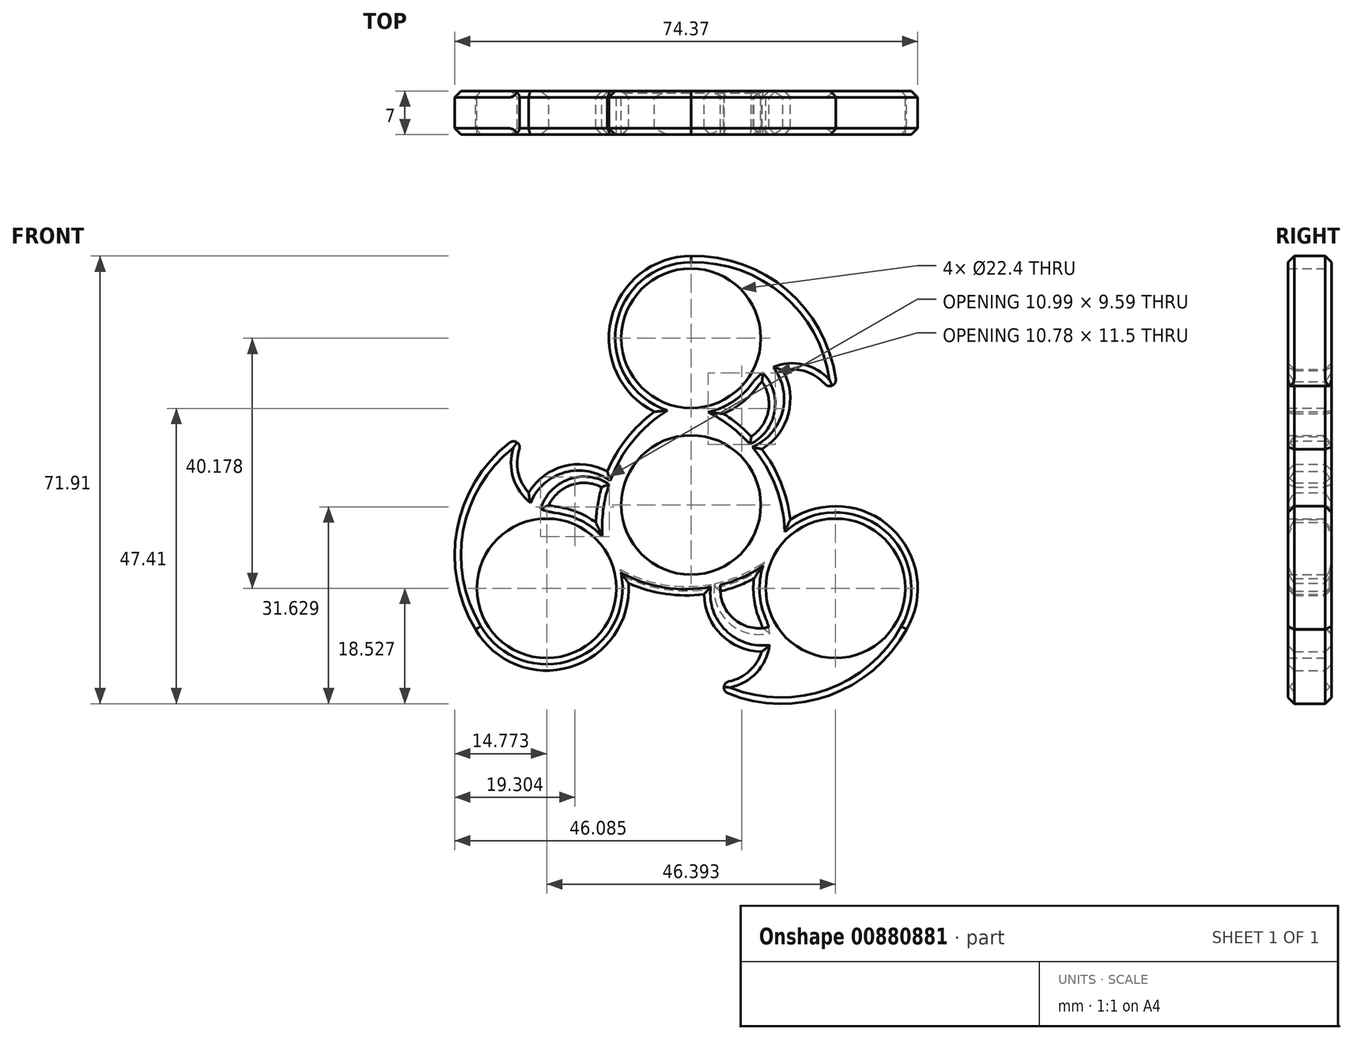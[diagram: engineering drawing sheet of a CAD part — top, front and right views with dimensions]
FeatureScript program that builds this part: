
annotation { "Feature Type Name" : "Feature", "Feature Type Description" : "" }
export const myFeature = defineFeature(function(context is Context, id is Id, definition is map)
    precondition{}
    {
        {
            var Q0;
            Q0=qCreatedBy(makeId("Front.planeOp"),FACE);
            var sketch = newSketch(context, id + "F0", { "sketchPlane" : qUnion([Q0])});
            skCircle(sketch, "E0", {"center": v(0, 0) * mm, "radius": 11.2 * mm});
            skCircle(sketch, "E1", {"center": v(0, 26.79) * mm, "radius": 13.2 * mm});
            skCircle(sketch, "E2", {"center": v(0, 26.79) * mm, "radius": 11.2 * mm});
            skCircle(sketch, "E3.1.0", {"center": v(-23.2, -13.4) * mm, "radius": 11.2 * mm});
            skCircle(sketch, "E3.1.1", {"center": v(-23.2, -13.4) * mm, "radius": 13.2 * mm});
            skCircle(sketch, "E3.2.0", {"center": v(23.2, -13.4) * mm, "radius": 11.2 * mm});
            skCircle(sketch, "E3.2.1", {"center": v(23.2, -13.4) * mm, "radius": 13.2 * mm});
            skArc(sketch, "E4", {"start": v(15.92, -2.38) * mm, "mid": v(12.5, 7.36) * mm, "end": v(5.2, 14.65) * mm});
            skArc(sketch, "E5.1.0", {"start": v(-5.9, 14.98) * mm, "mid": v(-12.62, 7.15) * mm, "end": v(-15.29, -2.82) * mm});
            skArc(sketch, "E5.2.0", {"start": v(-10.02, -12.6) * mm, "mid": v(0.12, -14.5) * mm, "end": v(10.09, -11.83) * mm});
            skArc(sketch, "E6", {"start": v(23.3, 14.22) * mm, "mid": v(17.54, 32.43) * mm, "end": v(0, 39.99) * mm});
            skArc(sketch, "E7", {"start": v(23.3, 14.22) * mm, "mid": v(18.73, 21.33) * mm, "end": v(10.62, 18.95) * mm});
            skArc(sketch, "E8.1.0", {"start": v(-23.97, 13.07) * mm, "mid": v(-27.83, 5.56) * mm, "end": v(-21.72, -0.28) * mm});
            skArc(sketch, "E8.1.1", {"start": v(-23.97, 13.07) * mm, "mid": v(-36.86, -1.02) * mm, "end": v(-34.63, -20) * mm});
            skArc(sketch, "E8.2.0", {"start": v(0.66, -27.3) * mm, "mid": v(9.1, -26.88) * mm, "end": v(11.1, -18.67) * mm});
            skArc(sketch, "E8.2.1", {"start": v(0.66, -27.3) * mm, "mid": v(19.32, -31.4) * mm, "end": v(34.63, -20) * mm});
            skArc(sketch, "E9", {"start": v(9.66, 11) * mm, "mid": v(12.4, 15.05) * mm, "end": v(11.4, 19.82) * mm});
            skArc(sketch, "E10", {"start": v(11.38, 8.98) * mm, "mid": v(15.62, 14.6) * mm, "end": v(14.75, 21.6) * mm});
            skArc(sketch, "E11.1.0", {"start": v(-14.36, 2.87) * mm, "mid": v(-19.23, 3.21) * mm, "end": v(-22.87, -0.04) * mm});
            skArc(sketch, "E11.1.1", {"start": v(-13.47, 5.37) * mm, "mid": v(-20.46, 6.22) * mm, "end": v(-26.08, 1.97) * mm});
            skArc(sketch, "E11.2.0", {"start": v(4.7, -13.87) * mm, "mid": v(6.83, -18.26) * mm, "end": v(11.47, -19.79) * mm});
            skArc(sketch, "E11.2.1", {"start": v(2.08, -14.35) * mm, "mid": v(4.84, -20.83) * mm, "end": v(11.34, -23.57) * mm});
            skSolve(sketch);
        }
        {
            var Q0;
            Q0 = qSketchRegion(id + "F0", true);
            extrude(context, id + "F1", {"entities" : qUnion([Q0]), "depth" : 7 * mm, "offsetDistance" : 25 * mm});
        }
        {
            var Q0;
            Q0=makeQuery(id+"F1.opExtrude","CAP_EDGE",EDGE,{"disambiguationData":[OSD([sQuery(id+"F0.wireOp",EDGE,"E8.1.1")])],"isStart":false});
            var Q1;
            {var subQ0=sQuery(id+"F0.wireOp",EDGE,"E3.1.1");Q1=makeQuery(id+"F1.opExtrude","CAP_EDGE",EDGE,{"disambiguationData":[OSD([subQ0]),TDD([makeQuery(id+"F0.imprint","IMPRINT",EDGE,{"disambiguationData":[TD([[makeQuery(id+"F0.imprint","INTERSECT",VERTEX,{"derivedFrom":[subQ0,sQuery(id+"F0.wireOp",EDGE,"E5.2.0")]}),1.0]])],"derivedFrom":subQ0})])],"isStart":false});}
            var Q2;
            Q2=makeQuery(id+"F1.opExtrude","CAP_EDGE",EDGE,{"disambiguationData":[OSD([sQuery(id+"F0.wireOp",EDGE,"E5.2.0")])],"isStart":true});
            var Q3;
            Q3=makeQuery(id+"F1.opExtrude","CAP_EDGE",EDGE,{"disambiguationData":[OSD([sQuery(id+"F0.wireOp",EDGE,"E5.2.0")])],"isStart":false});
            var Q4;
            Q4=makeQuery(id+"F1.opExtrude","CAP_EDGE",EDGE,{"disambiguationData":[OSD([sQuery(id+"F0.wireOp",EDGE,"E8.2.0")])],"isStart":false});
            var Q5;
            Q5=makeQuery(id+"F1.opExtrude","CAP_EDGE",EDGE,{"disambiguationData":[OSD([sQuery(id+"F0.wireOp",EDGE,"E8.2.1")])],"isStart":false});
            var Q6;
            {var subQ0=sQuery(id+"F0.wireOp",EDGE,"E3.2.1");Q6=makeQuery(id+"F1.opExtrude","CAP_EDGE",EDGE,{"disambiguationData":[OSD([subQ0]),TDD([makeQuery(id+"F0.imprint","IMPRINT",EDGE,{"disambiguationData":[TD([[makeQuery(id+"F0.imprint","INTERSECT",VERTEX,{"derivedFrom":[subQ0,sQuery(id+"F0.wireOp",EDGE,"E4")]}),1.0]])],"derivedFrom":subQ0})])],"isStart":false});}
            var Q7;
            Q7=makeQuery(id+"F1.opExtrude","CAP_EDGE",EDGE,{"disambiguationData":[OSD([sQuery(id+"F0.wireOp",EDGE,"E4")])],"isStart":false});
            var Q8;
            Q8=makeQuery(id+"F1.opExtrude","CAP_EDGE",EDGE,{"disambiguationData":[OSD([sQuery(id+"F0.wireOp",EDGE,"E7")])],"isStart":false});
            var Q9;
            Q9=makeQuery(id+"F1.opExtrude","CAP_EDGE",EDGE,{"disambiguationData":[OSD([sQuery(id+"F0.wireOp",EDGE,"E6")])],"isStart":false});
            var Q10;
            {var subQ0=sQuery(id+"F0.wireOp",EDGE,"E1");Q10=makeQuery(id+"F1.opExtrude","CAP_EDGE",EDGE,{"disambiguationData":[OSD([subQ0]),TDD([makeQuery(id+"F0.imprint","IMPRINT",EDGE,{"disambiguationData":[TD([[makeQuery(id+"F0.imprint","INTERSECT",VERTEX,{"derivedFrom":[subQ0,sQuery(id+"F0.wireOp",EDGE,"E5.1.0")]}),1.0]])],"derivedFrom":subQ0})])],"isStart":false});}
            var Q11;
            Q11=makeQuery(id+"F1.opExtrude","CAP_EDGE",EDGE,{"disambiguationData":[OSD([sQuery(id+"F0.wireOp",EDGE,"E5.1.0")])],"isStart":false});
            var Q12;
            Q12=makeQuery(id+"F1.opExtrude","CAP_EDGE",EDGE,{"disambiguationData":[OSD([sQuery(id+"F0.wireOp",EDGE,"E8.1.0")])],"isStart":false});
            var Q13;
            {var subQ0=sQuery(id+"F0.wireOp",EDGE,"E3.1.1");Q13=makeQuery(id+"F1.opExtrude","CAP_EDGE",EDGE,{"disambiguationData":[OSD([subQ0]),TDD([makeQuery(id+"F0.imprint","IMPRINT",EDGE,{"disambiguationData":[TD([[makeQuery(id+"F0.imprint","INTERSECT",VERTEX,{"derivedFrom":[subQ0,sQuery(id+"F0.wireOp",EDGE,"E5.1.0")]}),-1.0]])],"derivedFrom":subQ0})])],"isStart":false});}
            var Q14;
            {var subQ0=sQuery(id+"F0.wireOp",EDGE,"E1");Q14=makeQuery(id+"F1.opExtrude","CAP_EDGE",EDGE,{"disambiguationData":[OSD([subQ0]),TDD([makeQuery(id+"F0.imprint","IMPRINT",EDGE,{"disambiguationData":[TD([[makeQuery(id+"F0.imprint","INTERSECT",VERTEX,{"derivedFrom":[subQ0,sQuery(id+"F0.wireOp",EDGE,"E4")]}),-1.0]])],"derivedFrom":subQ0})])],"isStart":false});}
            var Q15;
            Q15=makeQuery(id+"F1.opExtrude","CAP_EDGE",EDGE,{"disambiguationData":[OSD([sQuery(id+"F0.wireOp",EDGE,"E10")])],"isStart":false});
            var Q16;
            Q16=makeQuery(id+"F1.opExtrude","CAP_EDGE",EDGE,{"disambiguationData":[OSD([sQuery(id+"F0.wireOp",EDGE,"E11.1.1")])],"isStart":false});
            var Q17;
            Q17=makeQuery(id+"F1.opExtrude","CAP_EDGE",EDGE,{"disambiguationData":[OSD([sQuery(id+"F0.wireOp",EDGE,"E11.2.1")])],"isStart":false});
            var Q18;
            Q18=makeQuery(id+"F1.opExtrude","CAP_EDGE",EDGE,{"disambiguationData":[OSD([sQuery(id+"F0.wireOp",EDGE,"E11.1.0")])],"isStart":false});
            var Q19;
            {var subQ0=sQuery(id+"F0.wireOp",EDGE,"E3.2.1");Q19=makeQuery(id+"F1.opExtrude","CAP_EDGE",EDGE,{"disambiguationData":[OSD([subQ0]),TDD([makeQuery(id+"F0.imprint","IMPRINT",EDGE,{"disambiguationData":[TD([[makeQuery(id+"F0.imprint","INTERSECT",VERTEX,{"derivedFrom":[subQ0,sQuery(id+"F0.wireOp",EDGE,"E5.2.0")]}),-1.0]])],"derivedFrom":subQ0})])],"isStart":false});}
            var Q20;
            Q20=makeQuery(id+"F1.opExtrude","CAP_EDGE",EDGE,{"disambiguationData":[OSD([sQuery(id+"F0.wireOp",EDGE,"E9")])],"isStart":false});
            chamfer(context, id + "F2", {"entities" : qUnion([Q0, Q1, Q2, Q3, Q4, Q5, Q6, Q7, Q8, Q9, Q10, Q11, Q12, Q13, Q14, Q15, Q16, Q17, Q18, Q19, Q20]), "width" : 1 * mm, "tangentPropagation" : true});
        }
        {
            var Q0;
            {var subQ0=sQuery(id+"F0.wireOp",EDGE,"E1");Q0=makeQuery(id+"F1.opExtrude","CAP_EDGE",EDGE,{"disambiguationData":[OSD([subQ0]),TDD([makeQuery(id+"F0.imprint","IMPRINT",EDGE,{"disambiguationData":[TD([[makeQuery(id+"F0.imprint","INTERSECT",VERTEX,{"derivedFrom":[subQ0,sQuery(id+"F0.wireOp",EDGE,"E5.1.0")]}),1.0]])],"derivedFrom":subQ0})])],"isStart":true});}
            var Q1;
            Q1=makeQuery(id+"F1.opExtrude","CAP_EDGE",EDGE,{"disambiguationData":[OSD([sQuery(id+"F0.wireOp",EDGE,"E6")])],"isStart":true});
            var Q2;
            Q2=makeQuery(id+"F1.opExtrude","CAP_EDGE",EDGE,{"disambiguationData":[OSD([sQuery(id+"F0.wireOp",EDGE,"E7")])],"isStart":true});
            var Q3;
            Q3=makeQuery(id+"F1.opExtrude","CAP_EDGE",EDGE,{"disambiguationData":[OSD([sQuery(id+"F0.wireOp",EDGE,"E4")])],"isStart":true});
            var Q4;
            {var subQ0=sQuery(id+"F0.wireOp",EDGE,"E1");Q4=makeQuery(id+"F1.opExtrude","CAP_EDGE",EDGE,{"disambiguationData":[OSD([subQ0]),TDD([makeQuery(id+"F0.imprint","IMPRINT",EDGE,{"disambiguationData":[TD([[makeQuery(id+"F0.imprint","INTERSECT",VERTEX,{"derivedFrom":[subQ0,sQuery(id+"F0.wireOp",EDGE,"E4")]}),-1.0]])],"derivedFrom":subQ0})])],"isStart":true});}
            var Q5;
            {var subQ0=sQuery(id+"F0.wireOp",EDGE,"E3.2.1");Q5=makeQuery(id+"F1.opExtrude","CAP_EDGE",EDGE,{"disambiguationData":[OSD([subQ0]),TDD([makeQuery(id+"F0.imprint","IMPRINT",EDGE,{"disambiguationData":[TD([[makeQuery(id+"F0.imprint","INTERSECT",VERTEX,{"derivedFrom":[subQ0,sQuery(id+"F0.wireOp",EDGE,"E4")]}),1.0]])],"derivedFrom":subQ0})])],"isStart":true});}
            var Q6;
            Q6=makeQuery(id+"F1.opExtrude","CAP_EDGE",EDGE,{"disambiguationData":[OSD([sQuery(id+"F0.wireOp",EDGE,"E8.2.1")])],"isStart":true});
            var Q7;
            Q7=makeQuery(id+"F1.opExtrude","CAP_EDGE",EDGE,{"disambiguationData":[OSD([sQuery(id+"F0.wireOp",EDGE,"E8.2.0")])],"isStart":true});
            var Q8;
            {var subQ0=sQuery(id+"F0.wireOp",EDGE,"E3.2.1");Q8=makeQuery(id+"F1.opExtrude","CAP_EDGE",EDGE,{"disambiguationData":[OSD([subQ0]),TDD([makeQuery(id+"F0.imprint","IMPRINT",EDGE,{"disambiguationData":[TD([[makeQuery(id+"F0.imprint","INTERSECT",VERTEX,{"derivedFrom":[subQ0,sQuery(id+"F0.wireOp",EDGE,"E5.2.0")]}),-1.0]])],"derivedFrom":subQ0})])],"isStart":true});}
            var Q9;
            {var subQ0=sQuery(id+"F0.wireOp",EDGE,"E5.2.0");Q9=makeQuery(id+"F2.opChamfer","BLEND_EDGE",EDGE,{"blendedFrom":[makeQuery(id+"F1.opExtrude","CAP_EDGE",EDGE,{"disambiguationData":[OSD([subQ0])],"isStart":true}),makeQuery(id+"F1.opExtrude","CAP_FACE",FACE,{"disambiguationData":[OSD([sQuery(id+"F0.wireOp",EDGE,"HtMsAHlR-RAXa-j7T0-fO2J-CcR4gQRzdXqi"),sQuery(id+"F0.wireOp",EDGE,"E1"),sQuery(id+"F0.wireOp",EDGE,"E2"),sQuery(id+"F0.wireOp",EDGE,"E3.1.0"),sQuery(id+"F0.wireOp",EDGE,"E3.1.1"),sQuery(id+"F0.wireOp",EDGE,"E3.2.0"),sQuery(id+"F0.wireOp",EDGE,"E3.2.1"),sQuery(id+"F0.wireOp",EDGE,"E4"),sQuery(id+"F0.wireOp",EDGE,"E5.1.0"),subQ0,sQuery(id+"F0.wireOp",EDGE,"E6"),sQuery(id+"F0.wireOp",EDGE,"E7"),sQuery(id+"F0.wireOp",EDGE,"E8.1.0"),sQuery(id+"F0.wireOp",EDGE,"E8.1.1"),sQuery(id+"F0.wireOp",EDGE,"E8.2.0"),sQuery(id+"F0.wireOp",EDGE,"E8.2.1")])],"isStart":true})],"blendedInto":[makeQuery(id+"F1.opExtrude","CAP_FACE",FACE,{"disambiguationData":[OSD([sQuery(id+"F0.wireOp",EDGE,"HtMsAHlR-RAXa-j7T0-fO2J-CcR4gQRzdXqi"),sQuery(id+"F0.wireOp",EDGE,"E1"),sQuery(id+"F0.wireOp",EDGE,"E2"),sQuery(id+"F0.wireOp",EDGE,"E3.1.0"),sQuery(id+"F0.wireOp",EDGE,"E3.1.1"),sQuery(id+"F0.wireOp",EDGE,"E3.2.0"),sQuery(id+"F0.wireOp",EDGE,"E3.2.1"),sQuery(id+"F0.wireOp",EDGE,"E4"),sQuery(id+"F0.wireOp",EDGE,"E5.1.0"),subQ0,sQuery(id+"F0.wireOp",EDGE,"E6"),sQuery(id+"F0.wireOp",EDGE,"E7"),sQuery(id+"F0.wireOp",EDGE,"E8.1.0"),sQuery(id+"F0.wireOp",EDGE,"E8.1.1"),sQuery(id+"F0.wireOp",EDGE,"E8.2.0"),sQuery(id+"F0.wireOp",EDGE,"E8.2.1")])],"isStart":true})]});}
            var Q10;
            {var subQ0=sQuery(id+"F0.wireOp",EDGE,"E3.1.1");Q10=makeQuery(id+"F1.opExtrude","CAP_EDGE",EDGE,{"disambiguationData":[OSD([subQ0]),TDD([makeQuery(id+"F0.imprint","IMPRINT",EDGE,{"disambiguationData":[TD([[makeQuery(id+"F0.imprint","INTERSECT",VERTEX,{"derivedFrom":[subQ0,sQuery(id+"F0.wireOp",EDGE,"E5.2.0")]}),1.0]])],"derivedFrom":subQ0})])],"isStart":true});}
            var Q11;
            Q11=makeQuery(id+"F1.opExtrude","CAP_EDGE",EDGE,{"disambiguationData":[OSD([sQuery(id+"F0.wireOp",EDGE,"E8.1.1")])],"isStart":true});
            var Q12;
            Q12=makeQuery(id+"F1.opExtrude","CAP_EDGE",EDGE,{"disambiguationData":[OSD([sQuery(id+"F0.wireOp",EDGE,"E8.1.0")])],"isStart":true});
            var Q13;
            Q13=makeQuery(id+"F1.opExtrude","CAP_EDGE",EDGE,{"disambiguationData":[OSD([sQuery(id+"F0.wireOp",EDGE,"E5.1.0")])],"isStart":true});
            var Q14;
            {var subQ0=sQuery(id+"F0.wireOp",EDGE,"E3.1.1");Q14=makeQuery(id+"F1.opExtrude","CAP_EDGE",EDGE,{"disambiguationData":[OSD([subQ0]),TDD([makeQuery(id+"F0.imprint","IMPRINT",EDGE,{"disambiguationData":[TD([[makeQuery(id+"F0.imprint","INTERSECT",VERTEX,{"derivedFrom":[subQ0,sQuery(id+"F0.wireOp",EDGE,"E5.1.0")]}),-1.0]])],"derivedFrom":subQ0})])],"isStart":true});}
            var Q15;
            Q15=makeQuery(id+"F1.opExtrude","CAP_EDGE",EDGE,{"disambiguationData":[OSD([sQuery(id+"F0.wireOp",EDGE,"E11.2.0")])],"isStart":true});
            var Q16;
            Q16=makeQuery(id+"F1.opExtrude","CAP_EDGE",EDGE,{"disambiguationData":[OSD([sQuery(id+"F0.wireOp",EDGE,"E9")])],"isStart":true});
            var Q17;
            Q17=makeQuery(id+"F1.opExtrude","CAP_EDGE",EDGE,{"disambiguationData":[OSD([sQuery(id+"F0.wireOp",EDGE,"E11.1.0")])],"isStart":true});
            var Q18;
            Q18=makeQuery(id+"F1.opExtrude","CAP_EDGE",EDGE,{"disambiguationData":[OSD([sQuery(id+"F0.wireOp",EDGE,"E10")])],"isStart":true});
            var Q19;
            Q19=makeQuery(id+"F1.opExtrude","CAP_EDGE",EDGE,{"disambiguationData":[OSD([sQuery(id+"F0.wireOp",EDGE,"E11.1.1")])],"isStart":true});
            var Q20;
            Q20=makeQuery(id+"F1.opExtrude","CAP_EDGE",EDGE,{"disambiguationData":[OSD([sQuery(id+"F0.wireOp",EDGE,"E11.2.1")])],"isStart":true});
            chamfer(context, id + "F3", {"entities" : qUnion([Q0, Q1, Q2, Q3, Q4, Q5, Q6, Q7, Q8, Q9, Q10, Q11, Q12, Q13, Q14, Q15, Q16, Q17, Q18, Q19, Q20]), "width" : 1 * mm, "tangentPropagation" : true});
        }
        {
            var Q0;
            Q0=makeQuery(id+"F1.opExtrude","SWEPT_EDGE",EDGE,{"disambiguationData":[OSD([sQuery(id+"F0.wireOp",EDGE,"E6"),sQuery(id+"F0.wireOp",EDGE,"E7")])]});
            var Q1;
            Q1=makeQuery(id+"F1.opExtrude","SWEPT_EDGE",EDGE,{"disambiguationData":[OSD([sQuery(id+"F0.wireOp",EDGE,"E8.1.0"),sQuery(id+"F0.wireOp",EDGE,"E8.1.1")])]});
            fillet(context, id + "F4", {"entities" : qUnion([Q0, Q1]), "radius" : 1 * mm, "tangentPropagation" : true, "allowEdgeOverflow" : false});
        }
        {
            var Q0;
            Q0=makeQuery(id+"F1.opExtrude","SWEPT_EDGE",EDGE,{"disambiguationData":[OSD([sQuery(id+"F0.wireOp",EDGE,"E8.2.0"),sQuery(id+"F0.wireOp",EDGE,"E8.2.1")])]});
            fillet(context, id + "F5", {"entities" : qUnion([Q0]), "radius" : 1 * mm, "tangentPropagation" : true, "allowEdgeOverflow" : false});
        }
    });
